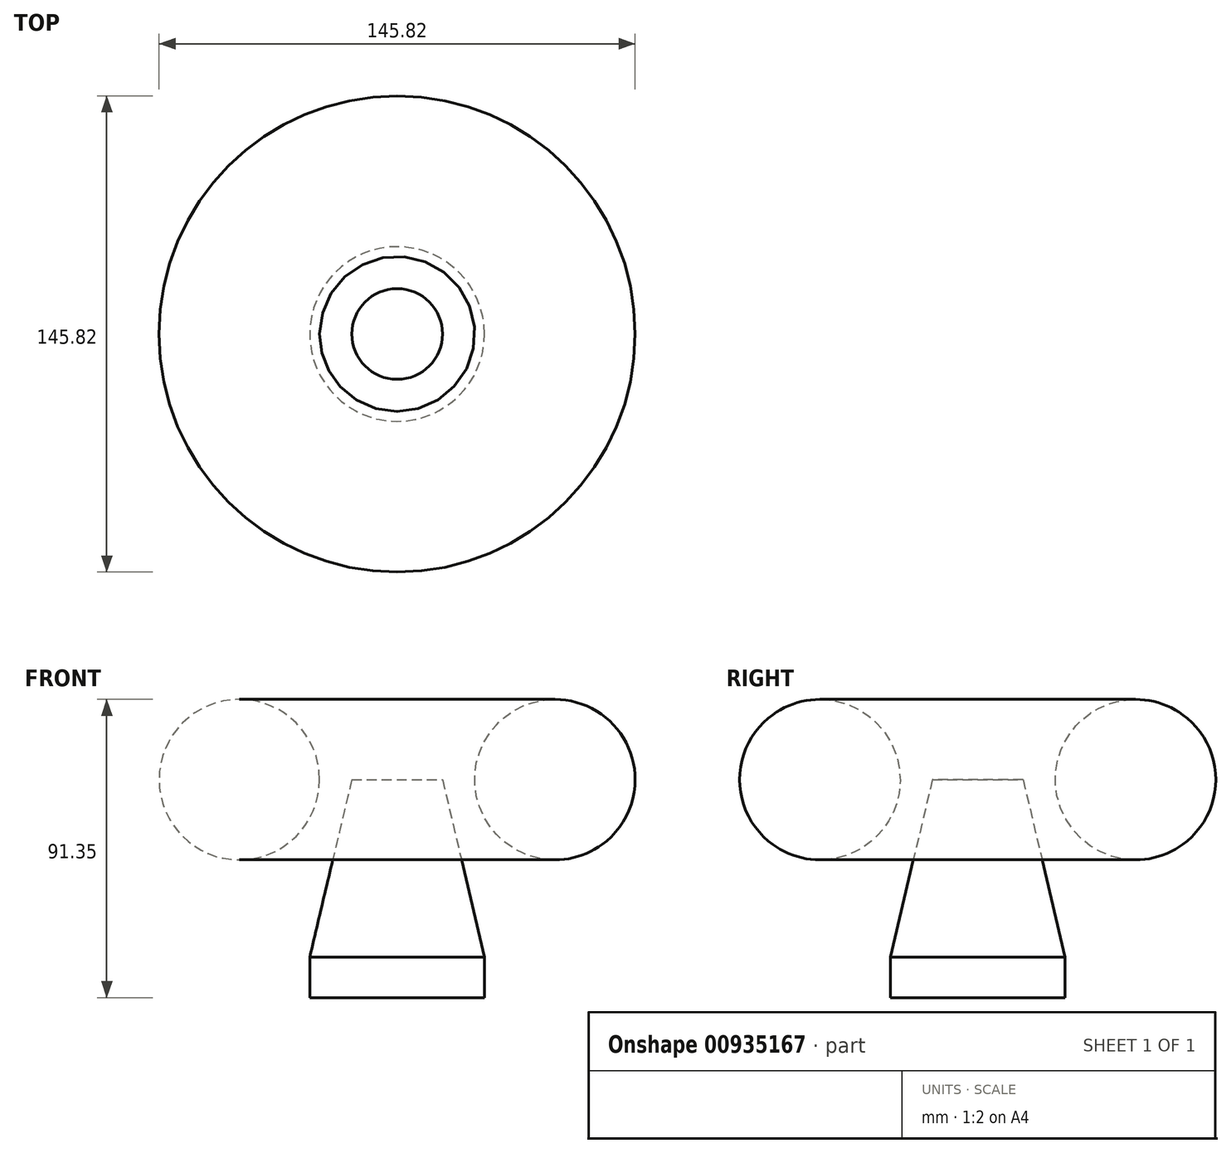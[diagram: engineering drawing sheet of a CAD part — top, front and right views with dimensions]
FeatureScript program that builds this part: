
annotation { "Feature Type Name" : "Feature", "Feature Type Description" : "" }
export const myFeature = defineFeature(function(context is Context, id is Id, definition is map)
    precondition{}
    {
        {
            var Q0;
            Q0=qCreatedBy(makeId("Front.planeOp"),FACE);
            var sketch = newSketch(context, id + "F0", { "sketchPlane" : qUnion([Q0])});
            skLineSegment(sketch, "E0", {"start": v(0, -66.77) * mm, "end": v(26.75, -66.77) * mm});
            skLineSegment(sketch, "E1", {"start": v(26.75, -66.77) * mm, "end": v(26.75, -54.31) * mm});
            skLineSegment(sketch, "E2", {"start": v(26.75, -54.31) * mm, "end": v(13.88, 0) * mm});
            skLineSegment(sketch, "E3", {"start": v(13.88, 0) * mm, "end": v(0, 0) * mm});
            skSolve(sketch);
        }
        {
            var Q0;
            Q0=qCreatedBy(makeId("Front.planeOp"),FACE);
            var sketch = newSketch(context, id + "F1", { "sketchPlane" : qUnion([Q0])});
            skLineSegment(sketch, "E4", {"start": v(0, 58.6) * mm, "end": v(0, -86.58) * mm});
            skSolve(sketch);
        }
        {
            var Q0;
            Q0 = qSketchRegion(id + "F3", true);
            var Q1;
            Q1=sQuery(id+"F0.wireOp",EDGE,"E0");
            var Q2;
            Q2=sQuery(id+"F0.wireOp",EDGE,"E2");
            var Q3;
            Q3=sQuery(id+"F0.wireOp",EDGE,"E1");
            var Q4;
            Q4=sQuery(id+"F0.wireOp",EDGE,"E3");
            var Q5;
            Q5=sQuery(id+"F1.wireOp",EDGE,"E4");
            revolve(context, id + "F2", {"bodyType" : ToolBodyType.SURFACE, "surfaceOperationType" : NewSurfaceOperationType.NEW, "entities" : qUnion([Q0]), "surfaceEntities" : qUnion([Q1, Q2, Q3, Q4]), "axis" : qUnion([Q5]), "revolveType" : RevolveType.FULL});
        }
        {
            var Q0;
            Q0=qCreatedBy(makeId("Front.planeOp"),FACE);
            var sketch = newSketch(context, id + "F3", { "sketchPlane" : qUnion([Q0])});
            skCircle(sketch, "E5", {"center": v(48.33, 0) * mm, "radius": 24.58 * mm});
            skSolve(sketch);
        }
        {
            var Q0;
            Q0=sQuery(id+"F3.wireOp",EDGE,"E5");
            var Q1;
            Q1=sQuery(id+"F1.wireOp",EDGE,"E4");
            revolve(context, id + "F4", {"bodyType" : ToolBodyType.SURFACE, "surfaceOperationType" : NewSurfaceOperationType.NEW, "surfaceEntities" : qUnion([Q0]), "axis" : qUnion([Q1]), "revolveType" : RevolveType.FULL});
        }
    });
